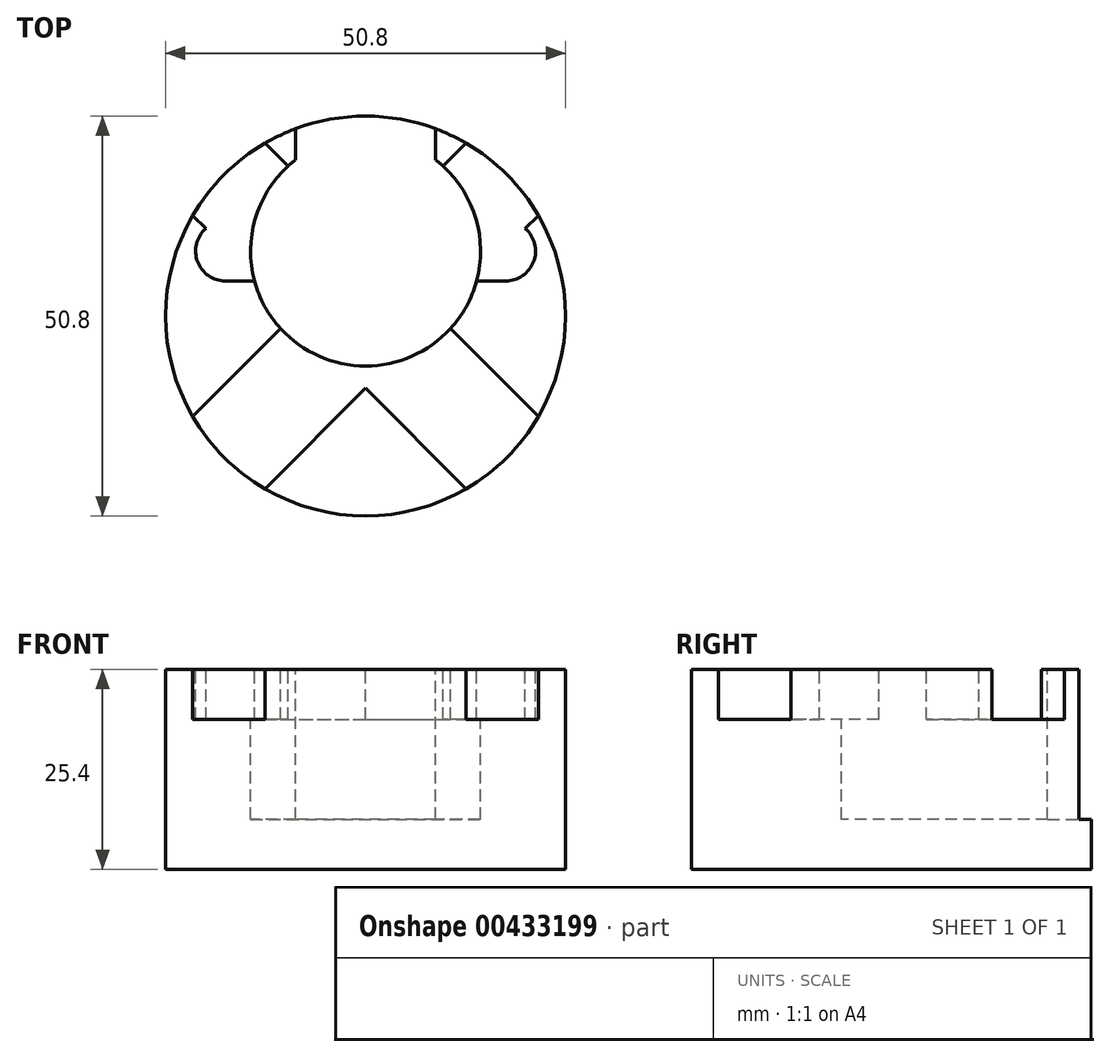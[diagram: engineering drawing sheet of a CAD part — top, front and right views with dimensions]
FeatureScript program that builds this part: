
annotation { "Feature Type Name" : "Feature", "Feature Type Description" : "" }
export const myFeature = defineFeature(function(context is Context, id is Id, definition is map)
    precondition{}
    {
        {
            var Q0;
            Q0=qCreatedBy(makeId("Top.planeOp"),FACE);
            var sketch = newSketch(context, id + "F0", { "sketchPlane" : qUnion([Q0])});
            skCircle(sketch, "E0", {"center": v(0, 0) * mm, "radius": 25.4 * mm});
            skSolve(sketch);
        }
        {
            var Q0;
            Q0 = qSketchRegion(id + "F0", true);
            extrude(context, id + "F1", {"entities" : qUnion([Q0]), "depth" : 25.4 * mm});
        }
        {
            var Q0;
            Q0=makeQuery(id+"F1.opExtrude","CAP_FACE",FACE,{"disambiguationData":[OSD([sQuery(id+"F0.wireOp",EDGE,"E0")])],"isStart":false});
            var sketch = newSketch(context, id + "F2", { "sketchPlane" : qUnion([Q0])});
            skCircle(sketch, "E1", {"center": v(0, 8.26) * mm, "radius": 14.6 * mm});
            skSolve(sketch);
        }
        {
            var Q0;
            Q0 = qSketchRegion(id + "F2", true);
            extrude(context, id + "F3", {"entities" : qUnion([Q0]), "operationType" : NewBodyOperationType.REMOVE, "oppositeDirection" : true, "depth" : 19.05 * mm});
        }
        {
            var Q0;
            Q0=qCreatedBy(makeId("Front.planeOp"),FACE);
            var sketch = newSketch(context, id + "F4", { "sketchPlane" : qUnion([Q0])});
            skLineSegment(sketch, "E2.bottom", {"start": v(3.81, 25.4) * mm, "end": v(-3.81, 25.4) * mm});
            skLineSegment(sketch, "E2.top", {"start": v(3.81, 21.6) * mm, "end": v(-3.81, 21.6) * mm});
            skLineSegment(sketch, "E2.left", {"start": v(3.8, 25.4) * mm, "end": v(3.8, 21.6) * mm});
            skLineSegment(sketch, "E2.right", {"start": v(-3.81, 25.4) * mm, "end": v(-3.81, 21.6) * mm});
            skPoint(sketch, "E3", {"position": v(0, 21.6) * mm});
            skPoint(sketch, "E4", {"position": v(0, 0) * mm});
            skSolve(sketch);
        }
        {
            var Q0;
            Q0 = qSketchRegion(id + "F4", true);
            extrude(context, id + "F5", {"entities" : qUnion([Q0]), "operationType" : NewBodyOperationType.REMOVE, "endBound" : BoundingType.THROUGH_ALL, "oppositeDirection" : true, "depth" : 25.4 * mm});
        }
        {
            var Q0;
            Q0=makeQuery(id+"F1.opExtrude","CAP_FACE",FACE,{"disambiguationData":[OSD([sQuery(id+"F0.wireOp",EDGE,"E0")])],"isStart":true});
            var sketch = newSketch(context, id + "F6", { "sketchPlane" : qUnion([Q0])});
            skCircle(sketch, "E5", {"center": v(0, 0) * mm, "radius": 26.67 * mm});
            skCircle(sketch, "E6", {"center": v(0, 0) * mm, "radius": 39.37 * mm});
            skSolve(sketch);
        }
        {
            var Q0;
            Q0=makeQuery(id+"F1.opExtrude","CAP_FACE",FACE,{"disambiguationData":[OSD([sQuery(id+"F0.wireOp",EDGE,"E0")])],"isStart":false});
            var sketch = newSketch(context, id + "F7", { "sketchPlane" : qUnion([Q0])});
            skLineSegment(sketch, "E7", {"start": v(0, 9.16) * mm, "end": v(-17.96, 27.12) * mm});
            skLineSegment(sketch, "E8", {"start": v(-17.96, 27.12) * mm, "end": v(-27.12, 17.96) * mm});
            skLineSegment(sketch, "E9", {"start": v(-27.12, 17.96) * mm, "end": v(-9.16, 0) * mm});
            skLineSegment(sketch, "E10", {"start": v(-9.16, 0) * mm, "end": v(-27.12, -17.96) * mm});
            skLineSegment(sketch, "E11", {"start": v(-27.12, -17.96) * mm, "end": v(-17.96, -27.12) * mm});
            skLineSegment(sketch, "E12", {"start": v(-17.96, -27.12) * mm, "end": v(0, -9.16) * mm});
            skLineSegment(sketch, "E13", {"start": v(0, -9.16) * mm, "end": v(17.96, -27.12) * mm});
            skLineSegment(sketch, "E14", {"start": v(17.96, -27.12) * mm, "end": v(27.12, -17.96) * mm});
            skLineSegment(sketch, "E15", {"start": v(27.12, -17.96) * mm, "end": v(9.16, 0) * mm});
            skLineSegment(sketch, "E16", {"start": v(9.16, 0) * mm, "end": v(27.12, 17.96) * mm});
            skLineSegment(sketch, "E17", {"start": v(27.12, 17.96) * mm, "end": v(17.96, 27.12) * mm});
            skLineSegment(sketch, "E18", {"start": v(17.96, 27.12) * mm, "end": v(0, 9.16) * mm});
            skSolve(sketch);
        }
        {
            var Q0;
            Q0 = qSketchRegion(id + "F7", true);
            extrude(context, id + "F8", {"entities" : qUnion([Q0]), "operationType" : NewBodyOperationType.REMOVE, "oppositeDirection" : true, "depth" : 6.35 * mm});
        }
        {
            var Q0;
            {var subQ0=sQuery(id+"F0.wireOp",EDGE,"E0");Q0=makeQuery(id+"F8.boolean.opBoolean","SPLIT",FACE,{"disambiguationData":[TD([makeQuery(id+"F8.opExtrude","SWEPT_FACE",FACE,{"disambiguationData":[OSD([sQuery(id+"F7.wireOp",EDGE,"E9")])]})])],"derivedFrom":makeQuery(id+"F1.opExtrude","CAP_FACE",FACE,{"disambiguationData":[OSD([subQ0])],"isStart":false})});}
            var sketch = newSketch(context, id + "F9", { "sketchPlane" : qUnion([Q0])});
            skLineSegment(sketch, "E19.bottom", {"start": v(-8.9, 26.67) * mm, "end": v(8.9, 26.67) * mm});
            skLineSegment(sketch, "E19.top", {"start": v(-8.9, 19.84) * mm, "end": v(8.9, 19.84) * mm});
            skLineSegment(sketch, "E19.left", {"start": v(-8.9, 26.67) * mm, "end": v(-8.9, 19.84) * mm});
            skLineSegment(sketch, "E19.right", {"start": v(8.89, 26.67) * mm, "end": v(8.89, 19.84) * mm});
            skPoint(sketch, "E20", {"position": v(0, -6.35) * mm});
            skSolve(sketch);
        }
        {
            var Q0;
            Q0 = qSketchRegion(id + "F9", true);
            var Q1;
            Q1=makeQuery(id+"F3.boolean.opBoolean","COPY",FACE,{"derivedFrom":makeQuery(id+"F3.opExtrude","CAP_FACE",FACE,{"disambiguationData":[OSD([sQuery(id+"F2.wireOp",EDGE,"E1")])],"isStart":false})});
            extrude(context, id + "F10", {"entities" : qUnion([Q0]), "operationType" : NewBodyOperationType.REMOVE, "endBound" : BoundingType.UP_TO_SURFACE, "oppositeDirection" : true, "depth" : 25.4 * mm, "endBoundEntityFace" : qUnion([Q1]), "offsetDistance" : 25.4 * mm});
        }
        {
            var Q0;
            {var subQ0=sQuery(id+"F0.wireOp",EDGE,"E0");Q0=makeQuery(id+"F8.boolean.opBoolean","SPLIT",FACE,{"disambiguationData":[TD([makeQuery(id+"F8.opExtrude","SWEPT_FACE",FACE,{"disambiguationData":[OSD([sQuery(id+"F7.wireOp",EDGE,"E9")])]})])],"derivedFrom":makeQuery(id+"F1.opExtrude","CAP_FACE",FACE,{"disambiguationData":[OSD([subQ0])],"isStart":false})});}
            var sketch = newSketch(context, id + "F11", { "sketchPlane" : qUnion([Q0])});
            skLineSegment(sketch, "E21", {"start": v(-17.78, 12.07) * mm, "end": v(17.78, 12.07) * mm});
            skLineSegment(sketch, "E22", {"start": v(-17.78, 4.45) * mm, "end": v(17.78, 4.45) * mm});
            skArc(sketch, "E23", {"start": v(-17.78, 12.06) * mm, "mid": v(-21.6, 8.25) * mm, "end": v(-17.78, 4.44) * mm});
            skArc(sketch, "E24", {"start": v(17.78, 4.45) * mm, "mid": v(21.6, 8.26) * mm, "end": v(17.78, 12.07) * mm});
            skLineSegment(sketch, "E25", {"start": v(-17.78, 8.26) * mm, "end": v(17.78, 8.26) * mm, "construction": true});
            skPoint(sketch, "E26", {"position": v(-21.6, 8.25) * mm});
            skPoint(sketch, "E27", {"position": v(21.6, 8.26) * mm});
            skPoint(sketch, "E28", {"position": v(0, 8.26) * mm});
            skSolve(sketch);
        }
        {
            var Q0;
            Q0 = qSketchRegion(id + "F11", true);
            var Q1;
            {var subQ0=sQuery(id+"F7.wireOp",EDGE,"E7");var subQ1=sQuery(id+"F7.wireOp",EDGE,"E9");Q1=makeQuery(id+"F8.boolean.opBoolean","COPY",FACE,{"disambiguationData":[TD([makeQuery(id+"F8.opExtrude","SWEPT_FACE",FACE,{"disambiguationData":[OSD([subQ0])]})])],"derivedFrom":makeQuery(id+"F8.opExtrude","CAP_FACE",FACE,{"disambiguationData":[OSD([subQ0,sQuery(id+"F7.wireOp",EDGE,"E8"),subQ1,sQuery(id+"F7.wireOp",EDGE,"E10"),sQuery(id+"F7.wireOp",EDGE,"E11"),sQuery(id+"F7.wireOp",EDGE,"E12"),sQuery(id+"F7.wireOp",EDGE,"E13"),sQuery(id+"F7.wireOp",EDGE,"E14"),sQuery(id+"F7.wireOp",EDGE,"E15"),sQuery(id+"F7.wireOp",EDGE,"E16"),sQuery(id+"F7.wireOp",EDGE,"E17"),sQuery(id+"F7.wireOp",EDGE,"E18")])],"isStart":false})});}
            extrude(context, id + "F12", {"entities" : qUnion([Q0]), "operationType" : NewBodyOperationType.REMOVE, "endBound" : BoundingType.UP_TO_SURFACE, "oppositeDirection" : true, "depth" : 25.4 * mm, "endBoundEntityFace" : qUnion([Q1]), "offsetDistance" : 25.4 * mm});
        }
    });
